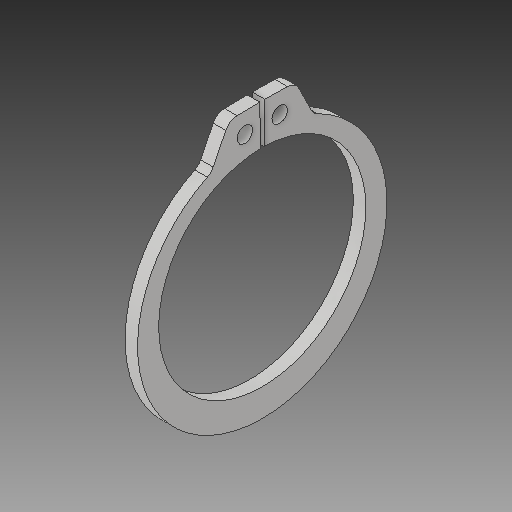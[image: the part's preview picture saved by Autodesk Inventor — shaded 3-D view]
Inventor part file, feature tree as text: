
AUTODESK INVENTOR PART (.ipt)
format: ipt  version: 2017 (Build 210142000, 142)  size: 101,376 bytes
history: native  units: in
note: dims shown in document units (in); Inventor stores cm internally (conversion verified against a paired STEP export)
features: fillet x1
ambient origin geometry x8: Origin, YZ Plane, XZ Plane, XY Plane, X Axis, Y Axis, Z Axis, Center Point
bodies: Solid1 (feature_tree)
feature tree (1):
  fillet  "Fillet1"  [1 undecoded]
note: 1 required parameter value undecoded (feature->parameter linkage not recoverable at this tier; creation-order binding heuristic only, values carry confidence <= 0.55)
